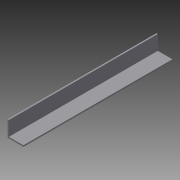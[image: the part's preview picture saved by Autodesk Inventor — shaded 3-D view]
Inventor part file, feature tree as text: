
AUTODESK INVENTOR PART (.ipt)
format: ipt  version: 2015 (Build 190159000, 159)  size: 78,848 bytes
history: native  units: in
note: dims shown in document units (in); Inventor stores cm internally (conversion verified against a paired STEP export)
features: extrude x2, sketch x2
ambient origin geometry x8: Origin, YZ Plane, XZ Plane, XY Plane, X Axis, Y Axis, Z Axis, Center Point
bodies: Solid1 (feature_tree)
feature tree (4):
  extrude  "Extrusion1"  Depth=0.125in
  extrude  "Extrusion2"  Depth=0.125in
  sketch  "Sketch1"  dims[d0=1.5in d1=0.125in]
  sketch  "Sketch2"  dims[d2=14.0in d3=0.0in d4=0.125in d5=1.5in d6=14.0in d7=0.0in]
